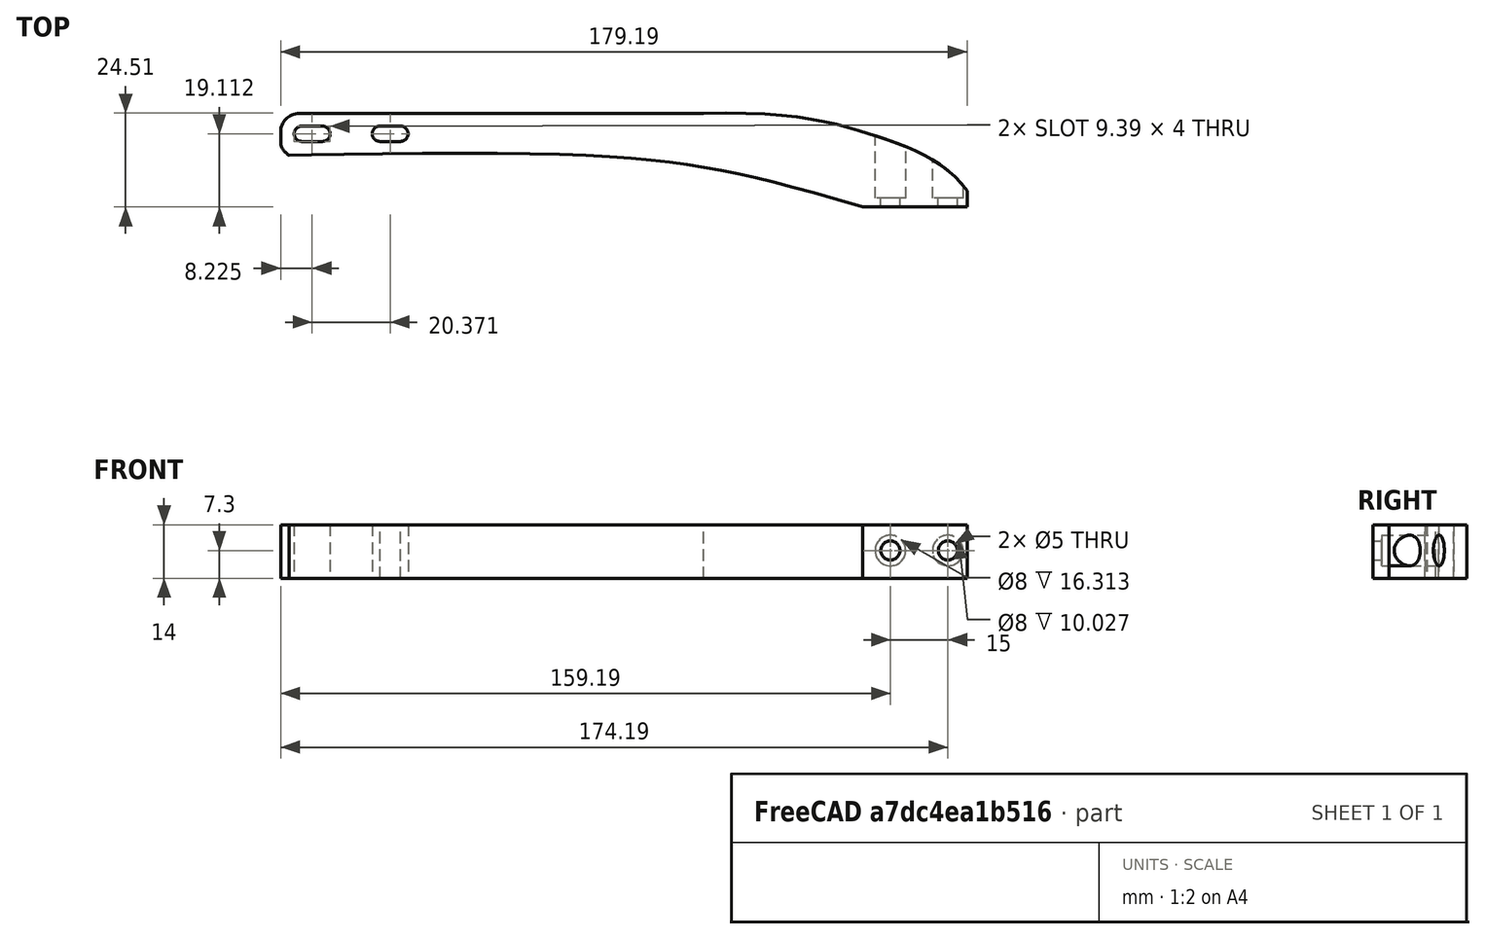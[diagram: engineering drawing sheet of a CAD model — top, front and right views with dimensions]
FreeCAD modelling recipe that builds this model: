
FCSTD DOCUMENT  (FreeCAD 0.18.4R)
Label: pittetter_motor_plate
License: All rights reserved
LicenseURL: http://en.wikipedia.org/wiki/All_rights_reserved
objects: App::Part×3, Mesh::Feature×2, Part::Cylinder×2, Part::FeaturePython×2, Part::Mirroring×2, PartDesign::Plane×1, Sketcher::SketchObject×1, PartDesign::Pad×1, PartDesign::Body×1, Part::MultiFuse×1, Part::Cut×1
note: 13 computed .brp shape members not serialized (recipe doc carries the construction recipe); baked Part::Feature solids carry a one-line shape summary decoded from their .brp

FEATURE [Mesh::Feature] compaund
  Placement = pos=(-17,2.1e-15,-2) rot=(0,0,1;3.14159rad)
FEATURE [Mesh::Feature] dragonlab_pipette_holder
  Placement = pos=(257,5.64e-14,43) rot=(-0.57735,0.57735,0.57735;4.18879rad)
FEATURE [App::Part] Part
  Group = -> [compaund,dragonlab_pipette_holder]
  Origin = -> Origin
  Placement = pos=(-50,0,0) rot=(0,0,1;0rad)
FEATURE [PartDesign::Plane] DatumPlane
  Length = 24
  MapMode = 2
  Placement = pos=(0,0,1) rot=(0,0,1;0rad)
  ResizeMode = 0
  Width = 24
FEATURE [Sketcher::SketchObject] Sketch
  MapMode = 5
  Placement = pos=(0,0,1) rot=(0,0,1;0rad)
  Support = -> [DatumPlane]
  sketch-geometry (23):
    g0: LineSegment StartX=86.8094 StartY=-23.7 StartZ=0 EndX=114 EndY=-23.7 EndZ=0
    g1: LineSegment StartX=45.214 StartY=-48.0939 StartZ=0 EndX=-60.3771 EndY=-48.0939 EndZ=0
    g2: ArcOfCircle CenterX=-59.6583 CenterY=-42.8122 CenterZ=0 NormalX=0 NormalY=0 NormalZ=1 AngleXU=0 Radius=2 StartAngle=1.5708 EndAngle=4.71239
    g3: ArcOfCircle CenterX=-54.2725 CenterY=-42.8122 CenterZ=0 NormalX=0 NormalY=0 NormalZ=1 AngleXU=0 Radius=2 StartAngle=4.71239 EndAngle=7.85398
    g4: LineSegment StartX=-59.6583 StartY=-44.8122 StartZ=0 EndX=-54.2725 EndY=-44.8122 EndZ=0
    g5: LineSegment StartX=-59.6583 StartY=-40.8122 StartZ=0 EndX=-54.2725 EndY=-40.8122 EndZ=0
    g6-g9: Circle [constr] x4 (B-spline internal-alignment scaffolding for g10; pole/knot coordinates omitted)
    g10: BSplineCurve PolesCount=5 KnotsCount=3 Degree=3 IsPeriodic=0
    g11: GeomPoint [constr] X=45.214 Y=-48.0939 Z=0
    g12: GeomPoint [constr] X=89.6545 Y=-42.4262 Z=0
    g13: Circle [constr] CenterX=85.6539 CenterY=-26.6221 CenterZ=0 NormalX=0 NormalY=0 NormalZ=1 AngleXU=0 Radius=2.83138
    g14: BSplineCurve PolesCount=4 KnotsCount=2 Degree=3 IsPeriodic=0
    g15: LineSegment StartX=-65.1889 StartY=-43.2821 StartZ=0 EndX=-65.1889 EndY=-40.0866 EndZ=0
    g16: LineSegment StartX=114 StartY=-23.7 StartZ=0 EndX=114 EndY=-27.9124 EndZ=0
    g17: ArcOfCircle CenterX=-60.3771 CenterY=-43.2821 CenterZ=0 NormalX=0 NormalY=0 NormalZ=1 AngleXU=0 Radius=4.81175 StartAngle=3.14159 EndAngle=4.71239
    g18: ArcOfCircle CenterX=-60.54 CenterY=-41.369 CenterZ=0 NormalX=0 NormalY=0 NormalZ=1 AngleXU=0 Radius=4.82255 StartAngle=2.10779 EndAngle=2.87244
    g19: ArcOfCircle CenterX=-39.2865 CenterY=-42.8122 CenterZ=0 NormalX=0 NormalY=0 NormalZ=1 AngleXU=0 Radius=2.0012 StartAngle=1.53615 EndAngle=4.74704
    g20: ArcOfCircle CenterX=-33.9019 CenterY=-42.8122 CenterZ=0 NormalX=0 NormalY=0 NormalZ=1 AngleXU=0 Radius=2.00125 StartAngle=4.74768 EndAngle=7.81869
    g21: LineSegment StartX=-39.2171 StartY=-44.8122 StartZ=0 EndX=-33.8313 EndY=-44.8122 EndZ=0
    g22: LineSegment StartX=-39.2171 StartY=-40.8122 StartZ=0 EndX=-33.8313 EndY=-40.8122 EndZ=0
  constraints (40):
    c: Horizontal(g0)
    c: Horizontal(g1)
    c: Tangent(g2,g5) = 1.5708
    c: Tangent(g2,g4) = -1.5708
    c: Tangent(g4,g3) = -1.5708
    c: Tangent(g5,g3) = 1.5708
    c: Horizontal(g4)
    c: Equal(g2,g3)
    c: DistanceY(g2,g2) = 4
    c: DistanceX(g-1,g0) = 114
    c: Coincident(g10,g1)
    c: Radius(g6) = 2
    c: Equal(g6,g7)
    c: Equal(g6,g8)
    c: Equal(g6,g9)
    c: InternalAlignment(g6-g9 -> g10) x4
    c: InternalAlignment(g11,g10)
    c: InternalAlignment(g12,g10)
    c: Coincident(g19,g22)
    c: Horizontal(g21)
    c: Horizontal(g22)
    c: Coincident(g22,g20)
    c: Coincident(g20,g21)
    c: DistanceX(g20,g20) = 0
    c: DistanceX(g19,g19) = 0
    c: Coincident(g21,g19)
    c: DistanceY(g20,g20) = 4
    c: DistanceY(g3,g19) = 0
    c: Equal(g5,g22)
    c: Coincident(g16,g10)
    c: Vertical(g16)
    c: Coincident(g0,g16)
    c: Coincident(g0,g14)
    c: Coincident(g18,g14)
    c: Coincident(g15,g17)
    c: Vertical(g15)
    c: Coincident(g18,g15)
    c: DistanceY(g0,g-1) = 23.7
    c: Tangent(g17,g15)
    c: Tangent(g1,g17) = 1.5708
FEATURE [PartDesign::Pad] Pad
  Length = 14
  Length2 = 100
  Placement = pos=(0,0,1) rot=(0,0,1;0rad)
  Profile = -> Sketch
  Type = 0
FEATURE [PartDesign::Body] Body
  Group = -> [DatumPlane,Sketch,Pad]
  Origin = -> Origin002
  Tip = -> Pad
FEATURE [Part::Cylinder] Cylinder
  Angle = 360
  AttacherType = Attacher::AttachEngine3D
  Height = 140
  Placement = pos=(0,0,0) rot=(1,0,0;1.5708rad)
  Radius = 2.5
FEATURE [Part::FeaturePython] Array  # Draft array (typed FeaturePython)
  Angle = 360
  ArrayType = 0
  Axis = (0,0,1)
  Base = -> Cylinder
  Center = (0,0,0)
  Fuse = false
  IntervalAxis = (0,0,0)
  IntervalX = (15,0,0)
  IntervalY = (0,1,0)
  IntervalZ = (0,0,1)
  NumberPolar = 1
  NumberX = 10
  NumberY = 1
  NumberZ = 1
  Placement = pos=(0,69,0) rot=(0,0,1;0rad)
FEATURE [Part::Cylinder] Cylinder001
  Angle = 360
  AttacherType = Attacher::AttachEngine3D
  Height = 30
  Placement = pos=(0,16,0) rot=(1,0,0;1.5708rad)
  Radius = 4
FEATURE [Part::FeaturePython] Array001  # Draft array (typed FeaturePython)
  Angle = 360
  ArrayType = 0
  Axis = (0,0,1)
  Base = -> Cylinder001
  Center = (0,0,0)
  Fuse = false
  IntervalAxis = (0,0,0)
  IntervalX = (15,0,0)
  IntervalY = (0,1,0)
  IntervalZ = (0,0,1)
  NumberPolar = 1
  NumberX = 10
  NumberY = 1
  NumberZ = 1
  Placement = pos=(0,-42,0) rot=(0,0,1;0rad)
FEATURE [Part::Mirroring] Part__Mirroring001  label="Array001 (Mirror #2)"
  Base = (0,20,0)
  Normal = (0,1,0)
  Placement = pos=(0,-41,0) rot=(0,0,1;0rad)
  Source = -> Array001
FEATURE [Part::MultiFuse] Fusion  label="hole row001"
  Placement = pos=(94,0,8.3) rot=(0,0,1;0rad)
  Shapes = -> [Array,Part__Mirroring001,Array001]
FEATURE [App::Part] Part004
  Group = -> [Array,Cylinder,Array001,Part__Mirroring001,Cylinder001,Fusion]
  Origin = -> Origin005
FEATURE [Part::Cut] Cut
  Base = -> Body
  Tool = -> Fusion
FEATURE [Part::Mirroring] Part__Mirroring  label="leg mirror"
  Base = (0,0,0)
  Normal = (0,1,0)
  Source = -> Cut
FEATURE [App::Part] Part001
  Group = -> [Body,Part__Mirroring]
  Origin = -> Origin001
